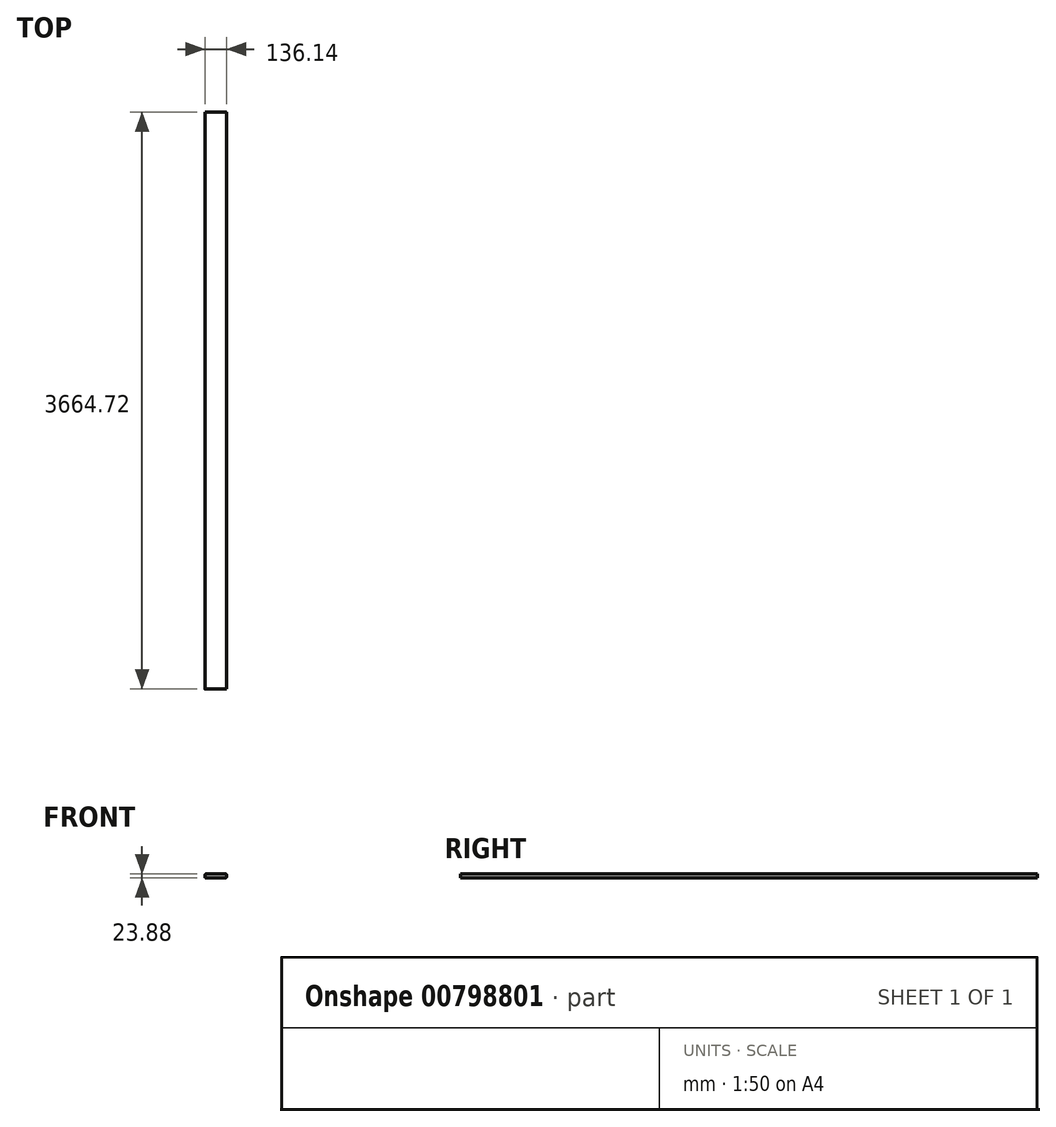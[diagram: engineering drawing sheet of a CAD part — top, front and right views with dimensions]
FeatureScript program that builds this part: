
annotation { "Feature Type Name" : "Feature", "Feature Type Description" : "" }
export const myFeature = defineFeature(function(context is Context, id is Id, definition is map)
    precondition{}
    {
        {
            var Q0;
            Q0=qCreatedBy(makeId("Front.planeOp"),FACE);
            var sketch = newSketch(context, id + "F0", { "sketchPlane" : qUnion([Q0])});
            skLineSegment(sketch, "E0.bottom", {"start": v(-63.25, 11.94) * mm, "end": v(63.25, 11.94) * mm});
            skLineSegment(sketch, "E0.top", {"start": v(-63.25, -11.94) * mm, "end": v(63.25, -11.94) * mm});
            skLineSegment(sketch, "E0.left", {"start": v(-68.07, 7.11) * mm, "end": v(-68.07, -7.11) * mm});
            skLineSegment(sketch, "E0.right", {"start": v(68.07, 7.11) * mm, "end": v(68.07, -7.11) * mm});
            skPoint(sketch, "E0.middle", {"position": v(0, 0) * mm});
            skPoint(sketch, "E1.visualSharp", {"position": v(-68.07, 11.94) * mm});
            skArc(sketch, "E1.filletArc", {"start": v(-63.25, 11.94) * mm, "mid": v(-66.66, 10.52) * mm, "end": v(-68.07, 7.11) * mm});
            skPoint(sketch, "E2.visualSharp", {"position": v(68.07, 11.94) * mm});
            skArc(sketch, "E2.filletArc", {"start": v(68.07, 7.11) * mm, "mid": v(66.66, 10.52) * mm, "end": v(63.25, 11.94) * mm});
            skPoint(sketch, "E3.visualSharp", {"position": v(68.07, -11.94) * mm});
            skArc(sketch, "E3.filletArc", {"start": v(63.25, -11.94) * mm, "mid": v(66.66, -10.52) * mm, "end": v(68.07, -7.11) * mm});
            skPoint(sketch, "E4.visualSharp", {"position": v(-68.07, -11.94) * mm});
            skArc(sketch, "E4.filletArc", {"start": v(-68.07, -7.11) * mm, "mid": v(-66.66, -10.52) * mm, "end": v(-63.25, -11.94) * mm});
            skSolve(sketch);
        }
        {
            var Q0;
            Q0=makeQuery(id+"F0.imprint","IMPRINT",FACE,{"disambiguationData":[TD([[makeQuery(id+"F0.imprint","IMPRINT",EDGE,{"derivedFrom":sQuery(id+"F0.wireOp",EDGE,"E0.bottom")}),-1.0]])]});
            extrude(context, id + "F1", {"entities" : qUnion([Q0]), "endBound" : BoundingType.SYMMETRIC, "depth" : 3664.71 * mm, "offsetDistance" : 25.4 * mm});
        }
    });
